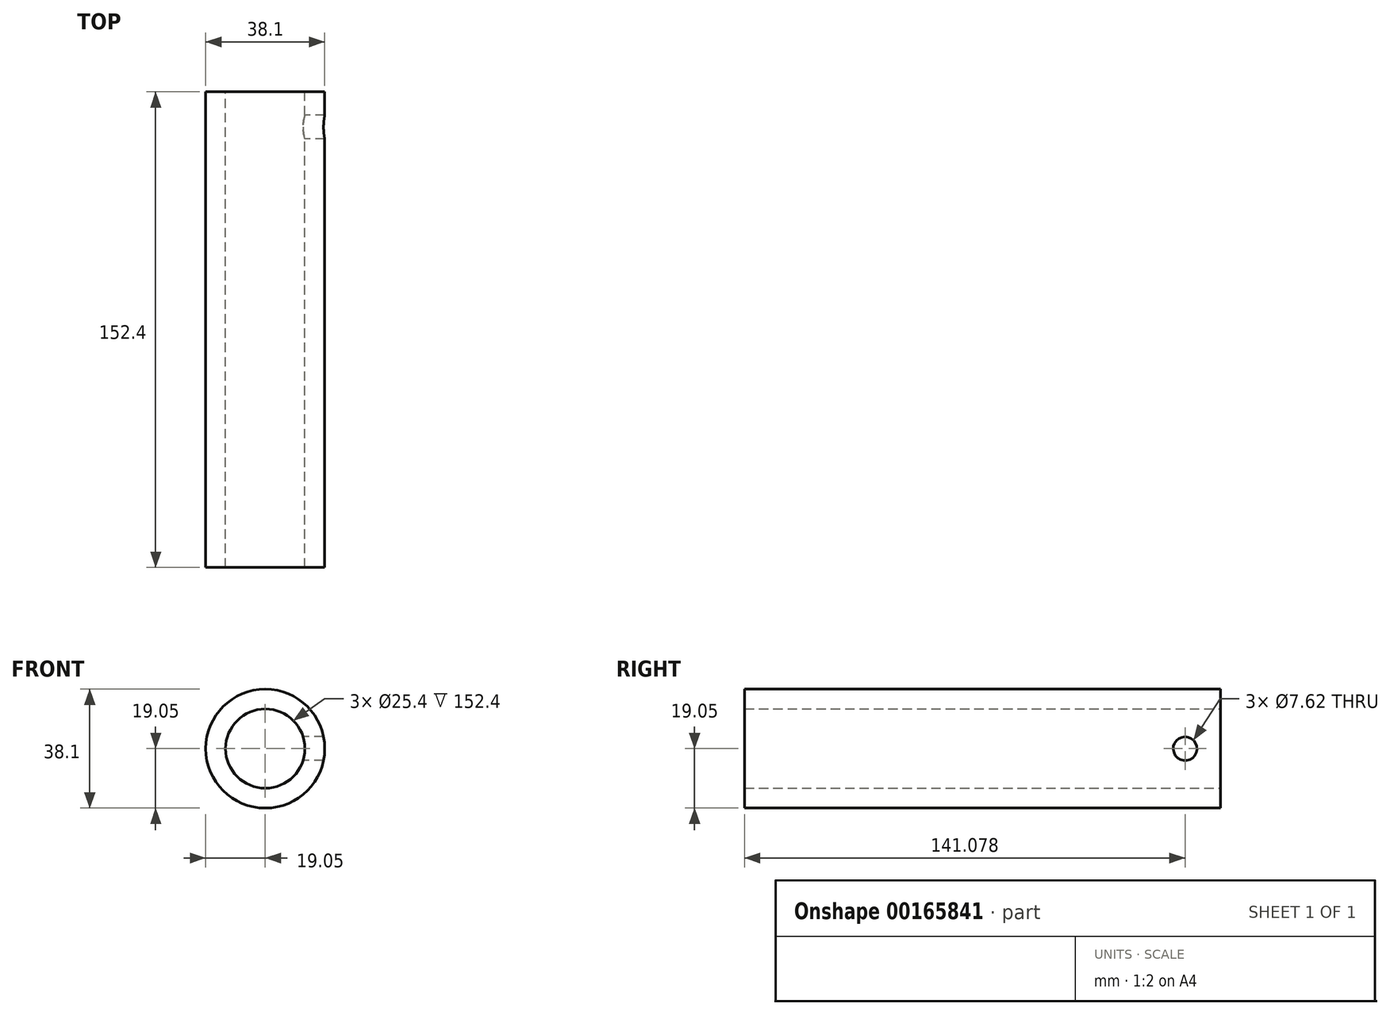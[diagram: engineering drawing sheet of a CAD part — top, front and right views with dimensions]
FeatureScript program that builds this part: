
annotation { "Feature Type Name" : "Feature", "Feature Type Description" : "" }
export const myFeature = defineFeature(function(context is Context, id is Id, definition is map)
    precondition{}
    {
        {
            var Q0;
            Q0=qCreatedBy(makeId("Front.planeOp"),FACE);
            var sketch = newSketch(context, id + "F0", { "sketchPlane" : qUnion([Q0])});
            skCircle(sketch, "E0", {"center": v(0, 0) * mm, "radius": 19.05 * mm});
            skCircle(sketch, "E1", {"center": v(0, 0) * mm, "radius": 12.7 * mm});
            skSolve(sketch);
        }
        {
            var Q0;
            Q0 = qSketchRegion(id + "F0", true);
            extrude(context, id + "F1", {"entities" : qUnion([Q0]), "endBound" : BoundingType.SYMMETRIC, "depth" : 152.4 * mm});
        }
        {
            var Q0;
            Q0=qCreatedBy(makeId("Right.planeOp"),FACE);
            var sketch = newSketch(context, id + "F2", { "sketchPlane" : qUnion([Q0])});
            skPoint(sketch, "E2", {"position": v(64.88, 0) * mm});
            skSolve(sketch);
        }
        {
            var Q0;
            Q0=sQuery(id+"F2.wireOp",VERTEX,"E2");
            var Q1;
            Q1=makeQuery(id+"F1.opExtrude","SWEPT_BODY",BODY,{"disambiguationData":[OSD([sQuery(id+"F0.wireOp",EDGE,"E0"),sQuery(id+"F0.wireOp",EDGE,"E1")])]});
            hole(context, id + "F3", {"style" : HoleStyle.SIMPLE, "endStyle" : HoleEndStyle.THROUGH, "oppositeDirection" : true, "holeDiameter" : 7.62 * mm, "startFromSketch" : true, "locations" : qUnion([Q0]), "scope" : qUnion([Q1]), "isTappedThrough" : true});
        }
    });
